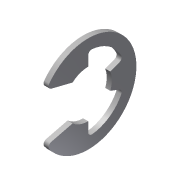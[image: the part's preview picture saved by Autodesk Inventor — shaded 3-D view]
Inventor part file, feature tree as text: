
AUTODESK INVENTOR PART (.ipt)
format: ipt  version: 2013 (Build 170138000, 138)  size: 97,792 bytes
history: native  units: in
note: dims shown in document units (in); Inventor stores cm internally (conversion verified against a paired STEP export)
features: fillet x1, other x1, imported_body x1
ambient origin geometry x8: Origin, YZ Plane, XZ Plane, XY Plane, X Axis, Y Axis, Z Axis, Center Point
feature tree (3):
  fillet  "Fillet1"  [1 undecoded]
  other  "217-2617-004 Rev1_97431A3401"
  imported_body  "Base1"
note: 1 required parameter value undecoded (feature->parameter linkage not recoverable at this tier; creation-order binding heuristic only, values carry confidence <= 0.55)
